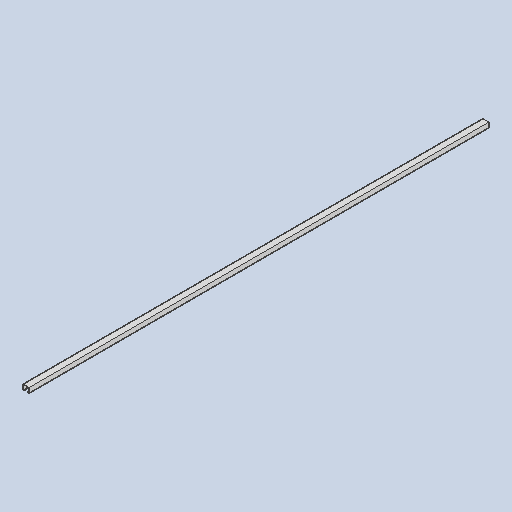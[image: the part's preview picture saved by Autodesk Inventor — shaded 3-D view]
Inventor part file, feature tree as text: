
AUTODESK INVENTOR PART (.ipt)
format: ipt  version: 2023 (Build 270158030, 158C)  size: 100,864 bytes
history: native  units: in
note: dims shown in document units (in); Inventor stores cm internally (conversion verified against a paired STEP export)
features: extrude x1, sketch x1
ambient origin geometry x8: Origin, YZ Plane, XZ Plane, XY Plane, X Axis, Y Axis, Z Axis, Center Point
bodies: Solid1 (feature_tree)
feature tree (2):
  extrude  "Extrusion1"  Depth=1.375in
  sketch  "Sketch1"  dims[d0=1.625in d1=1.375in d4=0.375in d5=0.2812in d6=0.1024in d7=0.1024in d8=0.1024in d9=0.1024in d11=0.1024in d12=0.1024in d13=0.2812in d14=0.1024in d15=120.0in d16=0.0in]
